# Revit family: Robe_Hook-DXV-Percy-D35105210_Series
name_source: partatom
category: Specialty Equipment
revit_build: Autodesk Revit 2014 (Build: 20130308_1515(x64)
units: mm (PartAtom-declared; Revit-internal decimal feet)

## types (2) — shared parameters
Assembly Code = C1030220
Default Elevation = 48"
Description = PERCY Robe Hook
Height = 2 1/4"
Installation Type = Wall Mounted
Length = 2 1/4"
Manufacturer = DXV
Price = Prices may vary. Please consult Manufacturer Representative for most up-to-date price list.
Product Documentation Link = http://dxv01.blob.core.windows.net
Product Page URL = http://www.dxv.com
URL = http://www.dxv.com
Warranty Information = Lifetime Limited Warranty
Width = 2 1/4"

## per-type parameters (varying)
| type | Finish | Material |
| D35105210.144 | Metal-DXV-144-Brushed Nickel | Metal-DXV-144-Brushed Nickel |
| D35105210.100 | Metal-DXV-100-Polished Chrome | Metal-DXV-100-Polished Chrome |

note: column(s) folded — value = type name in every type: Model

## geometry (parser evidence)
native form markers: Sweep x3
no freeform markers — native parametric forms only
